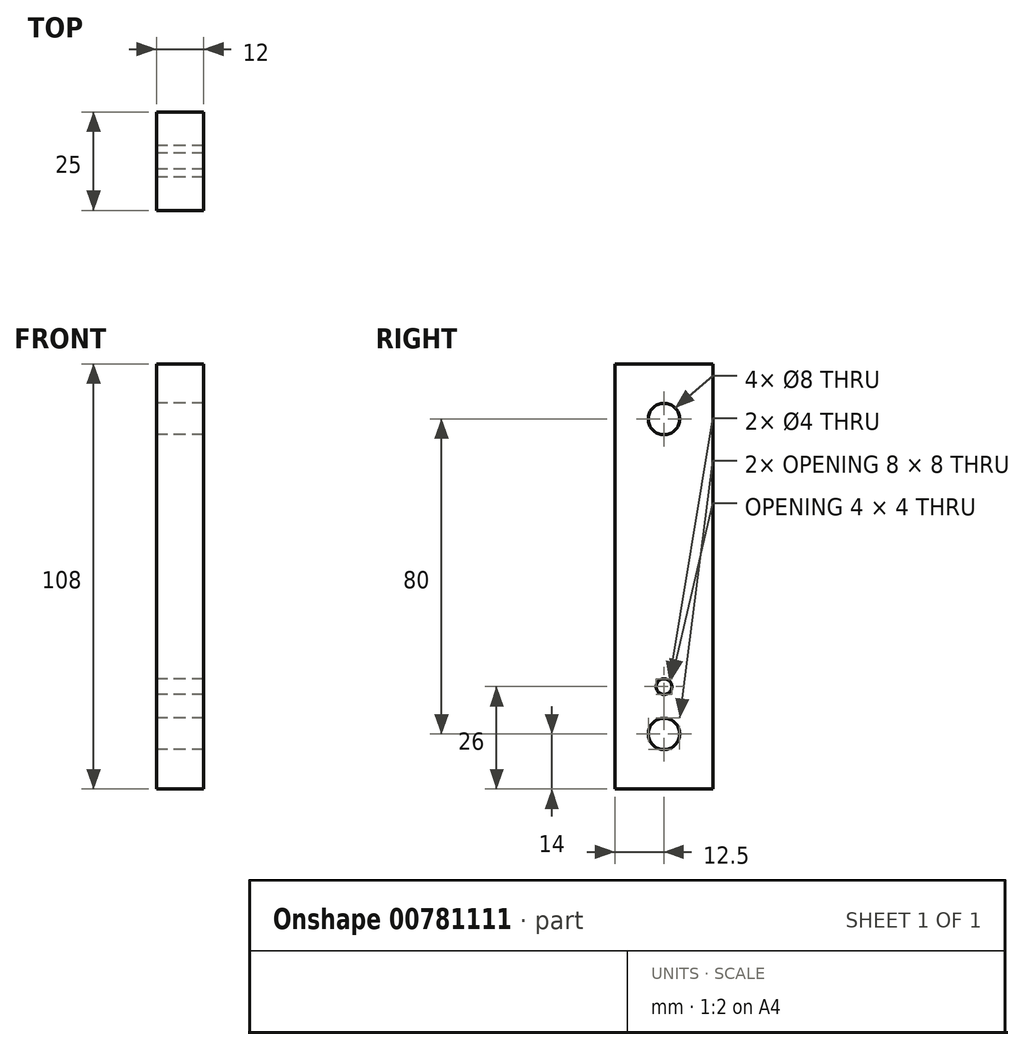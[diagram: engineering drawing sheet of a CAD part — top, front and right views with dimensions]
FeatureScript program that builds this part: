
annotation { "Feature Type Name" : "Feature", "Feature Type Description" : "" }
export const myFeature = defineFeature(function(context is Context, id is Id, definition is map)
    precondition{}
    {
        {
            var Q0;
            Q0=qCreatedBy(makeId("Right.planeOp"),FACE);
            var sketch = newSketch(context, id + "F0", { "sketchPlane" : qUnion([Q0])});
            skLineSegment(sketch, "E0.bottom", {"start": v(12.5, -54) * mm, "end": v(-12.5, -54) * mm});
            skLineSegment(sketch, "E0.top", {"start": v(12.5, 54) * mm, "end": v(-12.5, 54) * mm});
            skLineSegment(sketch, "E0.left", {"start": v(12.5, -54) * mm, "end": v(12.5, 54) * mm});
            skLineSegment(sketch, "E0.right", {"start": v(-12.5, -54) * mm, "end": v(-12.5, 54) * mm});
            skPoint(sketch, "E0.middle", {"position": v(0, 0) * mm});
            skLineSegment(sketch, "E1", {"start": v(0, 40) * mm, "end": v(0, -40) * mm, "construction": true});
            skPoint(sketch, "E2", {"position": v(0, -28) * mm});
            skSolve(sketch);
        }
        {
            var Q0;
            Q0 = qSketchRegion(id + "F0", true);
            extrude(context, id + "F1", {"entities" : qUnion([Q0]), "depth" : 12 * mm, "offsetDistance" : 25 * mm});
        }
        {
            var Q0;
            Q0=sQuery(id+"F0.wireOp",VERTEX,"E1.start");
            var Q1;
            Q1=sQuery(id+"F0.wireOp",VERTEX,"E1.end");
            var Q2;
            Q2=makeQuery(id+"F1.opExtrude","SWEPT_BODY",BODY,{"disambiguationData":[OSD([sQuery(id+"F0.wireOp",EDGE,"E0.bottom"),sQuery(id+"F0.wireOp",EDGE,"E0.top"),sQuery(id+"F0.wireOp",EDGE,"E0.left"),sQuery(id+"F0.wireOp",EDGE,"E0.right")])]});
            hole(context, id + "F2", {"style" : HoleStyle.SIMPLE, "endStyle" : HoleEndStyle.THROUGH, "oppositeDirection" : true, "holeDiameter" : 8 * mm, "majorDiameter" : 5 * mm, "isTappedThrough" : true, "tappedDepth" : 12 * mm, "tapClearance" : 3, "locations" : qUnion([Q0, Q1]), "scope" : qUnion([Q2])});
        }
        {
            var Q0;
            Q0=sQuery(id+"F0.wireOp",VERTEX,"E2");
            var Q1;
            Q1=makeQuery(id+"F1.opExtrude","SWEPT_BODY",BODY,{"disambiguationData":[OSD([sQuery(id+"F0.wireOp",EDGE,"E0.bottom"),sQuery(id+"F0.wireOp",EDGE,"E0.top"),sQuery(id+"F0.wireOp",EDGE,"E0.left"),sQuery(id+"F0.wireOp",EDGE,"E0.right")])]});
            hole(context, id + "F3", {"style" : HoleStyle.SIMPLE, "endStyle" : HoleEndStyle.THROUGH, "oppositeDirection" : true, "holeDiameter" : 4 * mm, "majorDiameter" : 5 * mm, "isTappedThrough" : true, "tappedDepth" : 12 * mm, "tapClearance" : 3, "locations" : qUnion([Q0]), "scope" : qUnion([Q1])});
        }
    });
